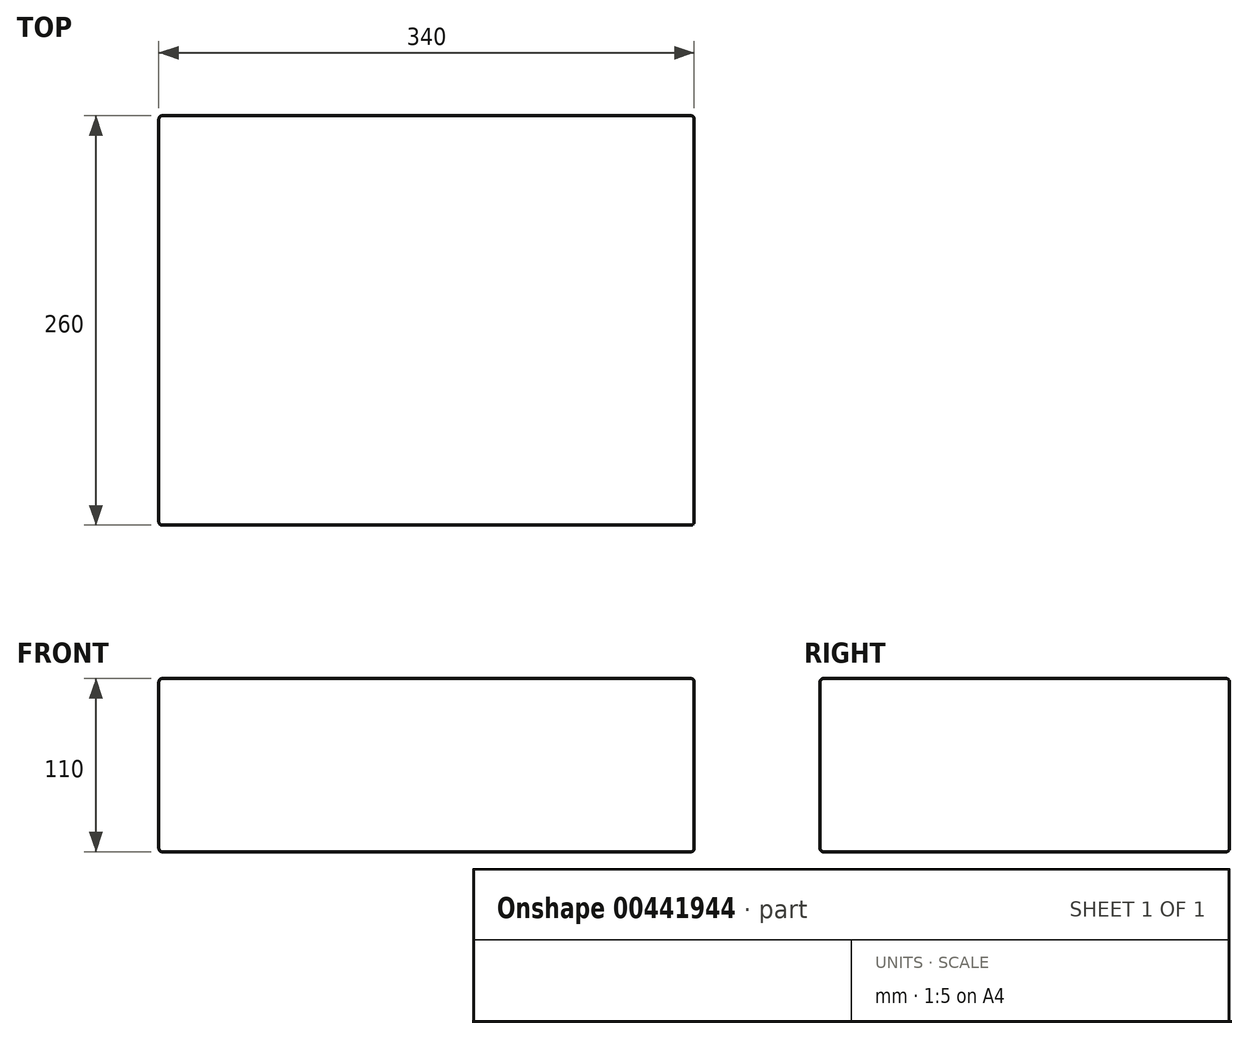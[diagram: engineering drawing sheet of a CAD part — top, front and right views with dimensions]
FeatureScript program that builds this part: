
annotation { "Feature Type Name" : "Feature", "Feature Type Description" : "" }
export const myFeature = defineFeature(function(context is Context, id is Id, definition is map)
    precondition{}
    {
        {
            var Q0;
            Q0=qCreatedBy(makeId("Top.planeOp"),FACE);
            var sketch = newSketch(context, id + "F0", { "sketchPlane" : qUnion([Q0])});
            skLineSegment(sketch, "E0.bottom", {"start": v(-170, -130) * mm, "end": v(170, -130) * mm});
            skLineSegment(sketch, "E0.top", {"start": v(-170, 130) * mm, "end": v(170, 130) * mm});
            skLineSegment(sketch, "E0.left", {"start": v(-170, -130) * mm, "end": v(-170, 130) * mm});
            skLineSegment(sketch, "E0.right", {"start": v(170, -130) * mm, "end": v(170, 130) * mm});
            skPoint(sketch, "E0.middle", {"position": v(0, 0) * mm});
            skSolve(sketch);
        }
        {
            var Q0;
            Q0 = qSketchRegion(id + "F0", true);
            extrude(context, id + "F1", {"entities" : qUnion([Q0]), "depth" : 110 * mm});
        }
        {
            var Q0;
            Q0=makeQuery(id+"F1.opExtrude","SWEPT_EDGE",EDGE,{"disambiguationData":[OSD([sQuery(id+"F0.wireOp",EDGE,"E0.top"),sQuery(id+"F0.wireOp",EDGE,"E0.right")])]});
            var Q1;
            Q1=makeQuery(id+"F1.opExtrude","SWEPT_EDGE",EDGE,{"disambiguationData":[OSD([sQuery(id+"F0.wireOp",EDGE,"E0.bottom"),sQuery(id+"F0.wireOp",EDGE,"E0.right")])]});
            var Q2;
            Q2=makeQuery(id+"F1.opExtrude","SWEPT_EDGE",EDGE,{"disambiguationData":[OSD([sQuery(id+"F0.wireOp",EDGE,"E0.bottom"),sQuery(id+"F0.wireOp",EDGE,"E0.left")])]});
            var Q3;
            Q3=makeQuery(id+"F1.opExtrude","CAP_EDGE",EDGE,{"disambiguationData":[OSD([sQuery(id+"F0.wireOp",EDGE,"E0.bottom")])],"isStart":true});
            var Q4;
            Q4=makeQuery(id+"F1.opExtrude","CAP_EDGE",EDGE,{"disambiguationData":[OSD([sQuery(id+"F0.wireOp",EDGE,"E0.bottom")])],"isStart":false});
            var Q5;
            Q5=makeQuery(id+"F1.opExtrude","CAP_EDGE",EDGE,{"disambiguationData":[OSD([sQuery(id+"F0.wireOp",EDGE,"E0.top")])],"isStart":false});
            var Q6;
            Q6=makeQuery(id+"F1.opExtrude","CAP_EDGE",EDGE,{"disambiguationData":[OSD([sQuery(id+"F0.wireOp",EDGE,"E0.left")])],"isStart":false});
            var Q7;
            Q7=makeQuery(id+"F1.opExtrude","CAP_EDGE",EDGE,{"disambiguationData":[OSD([sQuery(id+"F0.wireOp",EDGE,"E0.right")])],"isStart":true});
            var Q8;
            Q8=makeQuery(id+"F1.opExtrude","CAP_EDGE",EDGE,{"disambiguationData":[OSD([sQuery(id+"F0.wireOp",EDGE,"E0.right")])],"isStart":false});
            var Q9;
            Q9=makeQuery(id+"F1.opExtrude","SWEPT_EDGE",EDGE,{"disambiguationData":[OSD([sQuery(id+"F0.wireOp",EDGE,"E0.top"),sQuery(id+"F0.wireOp",EDGE,"E0.left")])]});
            var Q10;
            Q10=makeQuery(id+"F1.opExtrude","CAP_EDGE",EDGE,{"disambiguationData":[OSD([sQuery(id+"F0.wireOp",EDGE,"E0.top")])],"isStart":true});
            var Q11;
            Q11=makeQuery(id+"F1.opExtrude","CAP_EDGE",EDGE,{"disambiguationData":[OSD([sQuery(id+"F0.wireOp",EDGE,"E0.left")])],"isStart":true});
            fillet(context, id + "F2", {"entities" : qUnion([Q0, Q1, Q2, Q3, Q4, Q5, Q6, Q7, Q8, Q9, Q10, Q11]), "radius" : 2 * mm, "tangentPropagation" : true, "allowEdgeOverflow" : false});
        }
    });
